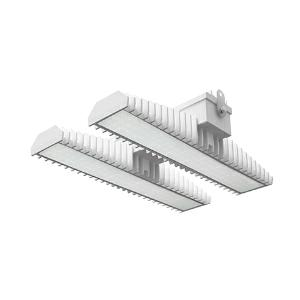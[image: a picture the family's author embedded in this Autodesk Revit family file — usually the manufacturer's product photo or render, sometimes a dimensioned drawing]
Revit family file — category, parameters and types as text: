
# Revit family: 3f_filippi_-_3f_lem_medio_3f_filippi_-_58911_a0812_-_3f_lem_2_led_100_dali_cr_medio___vs_bb8d
name_source: partatom
category: Lighting Fixtures
units: mm (PartAtom-declared; Revit-internal decimal feet)

## family parameters
Cut with Voids When Loaded = No
Host = Face
Light Source = No
Part Type = Normal
Room Calculation Point = No
Round Connector Dimension = Use Diameter
Shared = No

## types (1)
- 3F Filippi - 3F LEM Medio (1 x LED, 13466 lm, 109 W, 4000 K)
    Apparent Load = 109 VA
    Approval mark = CE
    CIE Flux Codes = 77 92 98 100 100
    Color Rendering = 80
    Color Temperature = 4000 K
    Control Gear = Electronic transformer
    Default Elevation = 1800 mm
    Description = Industrial luminaire with high light output and high luminous efficiency designed with the most innovative technologies for environments with temperature up to 55°C.

ILLUMINOTECHNICAL
Luminous efficiency 100% (DLOR 98%, ULOR 2%).
Initial luminous flux of the luminaire 13466 lm.
Medium distribution with rectangular shape.
Installation Interdistance Transv.D = 1.10 x hu - Long.D = 1.14 x hu.
Tabular UGR (CIE 117 - 4H-8H; S=0.25H; 70/50/20): RUG 20.5 - 20.4.
Beam angle: 58° - 57°.
Luminous efficacy 124 lm/W.
Lifetime (L93/B10): 30000 h. (tq+25°C)
Lifetime (L90/B10): 50000 h. (tq+25°C)
Lifetime (L85/B10): 80000 h. (tq+25°C)
Lifetime (L80/B10): 100000 h. (tq+25°C)
Lifetime (L85/B10): 50000 h. (tq+55°C)
Sudden decreased luminous flux after 50000 hours: 0% (C0).
Photobiological safety in compliance with IEC/TR 62778: RG0 risk exempt, (IEC 62471).
In compliance with IEC/EN 62722-2-1 - IEC/EN 62717 standards.

SOURCE
2 Mid-Power linear LED modules 50W/840.
Energy efficiency class (UE 2019/2020 - UE 2019/2015): C.
CIE 13.3 Colour rendering index: CRI >80 (R9 <50%).
IES TM-30 Fidelity Index: Rf = 84 Rg = 95.
CCT nominal colour temperature 4000 K.
Colour initial tolerance (MacAdam): SDCM 3.

MECHANICAL
Passive modular heatsinks in die-casted aluminium, painted in white colour.
To optimize the thermal management of the LED module, the heatsinks are oversized and provided with self-cleaning of cooling fins.
Wiring body in aluminium and galvanised steel anchored solidly to the sinks and thermally separated.
3F Lens lenses with high luminous efficiency, transparent methacrylate (PMMA), fixed to the LED modules.
Fixing brackets in stainless steel.
Luminaire with limited surface temperature. - D - (EN 60598-2-24)
Dimensions: 470x542 mm, height 133 mm. Weight 10.13 kg.
IP65 protection degree.
Mechanical strength to impacts IK06 (1 joule).
Glow-wire test resistance 650°C.

ELECTRICAL
Halogen Free DALI-2 DATI (Parts 251, 252, 253), PUSH-DIM, electronic wiring 230V-50/60Hz, power factor 0.97 at full load, THD <25%, constant output current, class I, 1 driver, 1 DALI addresse.
Power of the luminaire 109 W.
ENEC - CE.
Flicker: <4%.
Luminaire compliant with EN 60598-2-22 for power supply from a centralised emergency system CPSS (Central Power Supply System), not incorporated in the luminaire - high risk areas excluded. The default power and flux are 100% in AC and 15% in DC.
Ambient temperature from -30°C to +55°C.
Temperature class T6 max 85°C.
Quick connection via M25 5P connector with 9-13 mm tightening range.
Power unit positioned on a separate compartment by the LED module to ensure optimum temperatures of cabling components, to be inspectable and maintainable.
Relative humidity UR: <85%.

INSTALLATION
Ceiling / Suspended / Wall.
All accessories dedicated to this product are available on the Catalog and on our website www.3F-Filippi.com.

ACCESSORIES
A0812 - Anti-glare microprismatic VS moulded glass, tempered, not flammable, with sealing gasket.
One required for each light module. The pack contains 10 pieces.

APPLICATIONS
In commercial environments, exhibition and industrial areas, stores, open areas.
Applications with high ambient temperature up to 55°C.
Environments in which it is necessary a total protection against falling fragments (eg environments with foodstuffs or machines with moving parts or with extreme temperature changes), use luminaires with polycarbonate lenses.

LIGHT MANAGEMENT
Recommended minimum setting: 10%.
The luminaire, equipped with (DALI-2 DATI) driver, can be controlled manually with 3F Easy Dim technology or automatically/manually with wired or wireless DALI/D2D control systems.
The D2D driver guarantees interoperability with other devices with the same certification by making the following information available:
Device Data (Part 251), Energy Report (Part 252), Diagnosis & Maintenance (Part 253).
In electrical systems without a regulation system (manual or automatic) and DALI bus, a suitable jumper must be made on the DA-DA terminals of the appliance.

WARNING
Fixture not suitable for cold stores with an ambient temperature <0°C and/or relative humidity >85%.
Luminaire designed for disposal/recycling at end-of-life.
Replaceable (LED only) light source by a professional. Replaceable control gear by a professional.
    Height = 133 mm  [stored 0.436352 ft]
    Lamp = 1 x LED
    Lamp Light Flux = 13466 lm
    Lamp Power = 109 W
    Lamp count = 1
    Length = 470 mm
    Lifetime = 50000 h
    Luminous efficacy = 124 lm/W
    Manufacturer = 3F Filippi
    ModVariant = No
    Model = 3F Filippi - 58911+A0812 - 3F LEM 2 LED 100 DALI CR MEDIO + VS
    Mounting Place = Ceiling
    Mounting Type = Pendant
    Number of Poles = 1
    OnlyDefault = Yes
    Power Factor = 1
    Product Name = 3F Filippi - 3F LEM Medio
    Product group = pendant luminaire
    ProductGroupID = 9
    Protection Class = Protection class I
    Protection Degree = IP 65
    RLX_Detail_Level = 1
    RLX_Emergency_Light_Flux = 0 lm
    RLX_Emergency_Type = 0
    RLX_Emergency_Type_DB = No
    RlxData = <blob elided: 97449 chars, md5=c4100a62>
    Socket = socket
    Standby Power = 0 W
    System Light Flux = 13466 lm
    System Power = 109 W
    Type Comments = Product without accessories
    Type Image = 3f_filippi_-_lem_2__a0812.jpg
    URL = http://relux.com
    VarID = ---
    Voltage = 0 V
    Weight = 0.00 kg
    Width = 542 mm

note: [stored X ft] marks values corroborated as IEEE doubles in the binary element streams (Revit-internal decimal feet)

## geometry (parser evidence)
native form markers: Blend x4, Sweep x12
no freeform markers — native parametric forms only
